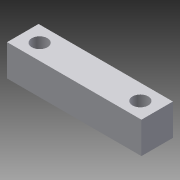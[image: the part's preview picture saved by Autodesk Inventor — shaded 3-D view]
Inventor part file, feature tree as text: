
AUTODESK INVENTOR PART (.ipt)
format: ipt  version: 2013 (Build 170138000, 138)  size: 82,944 bytes
history: native  units: mm
features: extrude x1, sketch x1
ambient origin geometry x8: Origin, YZ Plane, XZ Plane, XY Plane, X Axis, Y Axis, Z Axis, Center Point
bodies: Solid1 (feature_tree)
feature tree (2):
  extrude  "Extrusion1"  [1 undecoded]
  sketch  "Sketch1"  dims[d0=6.0mm d1=0.0mm]
note: 1 required parameter value undecoded (feature->parameter linkage not recoverable at this tier; creation-order binding heuristic only, values carry confidence <= 0.55)
